# Revit family: 63__LF_UN_Emilux_Arrondi_R17
name_source: partatom
category: Lighting Fixtures
revit_build: Autodesk Revit 2017 (Build: 20190508_0315(x64)
units: mm (PartAtom-declared; Revit-internal decimal feet)

## family parameters
Always vertical = Yes
Cut with Voids When Loaded = No
Light Source = Yes
Part Type = Normal
Room Calculation Point = No
Round Connector Dimension = Use Diameter
Shared = No
Work Plane-Based = No

## types (9) — shared parameters
Assembly Code = 63.0
Color Filter = 16777215
Comment = Initial color needs to be filled in manually
Dali = Yes
Dimming Lamp Color Temperature Shift = <None>
Height Coupling = 24 mm  [stored 0.0787402 ft]
IP = IP 54
IfcExportAs = IfcLightFixtureType
IfcExportType = POINTSOURCE
Lamp = LED
Manufacturer = Emilux
Material = Polycarbonaat
Tilt Angle = 90.00°
URL = https://www.emilux.nl

## per-type parameters (varying)
| type | Apparent Load | Bottom Outside | Description | Emergency Lighting | Height Total | Length Coupling | Model | Photometric Web File | Ring ID | Ring OD | Top OD | Wattage Comments | Width Coupling |
| LED 1090lm 3000K (13W) | 13 VA | 61 mm | Cutout Ø130mm | No | 82 mm  [stored 0.269029 ft] | 75 mm | Arrondi+ Downlighter 13W | Arrondi 13W Alu 300K.ies | 121 mm | 145 mm | 48 mm  [stored 0.15748 ft] | 13W | 34 mm  [stored 0.111549 ft] |
| LED 2280lm 3000K (18W) | 25 VA | 97 mm | Cutout Ø205mm | No | 98 mm  [stored 0.321522 ft] | 120 mm  [stored 0.393701 ft] | Arrondi+ Downlighter 25W | Arrondi 25W Alu 3000K.ies | 173 mm  [stored 0.567585 ft] | 228 mm  [stored 0.748031 ft] | 73 mm  [stored 0.239501 ft] | 25W | 45 mm  [stored 0.147638 ft] |
| LED 1300lm 4000K (13W) | 13 VA | 61 mm | Cutout Ø130mm | No | 82 mm  [stored 0.269029 ft] | 75 mm | Arrondi+ Downlighter 13W | Arrondi 13W Alu 4000K.ies | 121 mm | 145 mm | 48 mm  [stored 0.15748 ft] | 13W | 34 mm  [stored 0.111549 ft] |
| LED 1300lm 6000K (13W) | 13 VA | 61 mm | Cutout Ø130mm | No | 82 mm  [stored 0.269029 ft] | 75 mm | Arrondi+ Downlighter 13W | Arrondi 13W Alu 6000K.ies | 121 mm | 145 mm | 48 mm  [stored 0.15748 ft] | 13W | 34 mm  [stored 0.111549 ft] |
| LED 1300lm 3000K (18W) | 18 VA | 61 mm | Cutout Ø130 | No | 82 mm  [stored 0.269029 ft] | 75 mm | Arrondi+ Downlighter 13W | Arrondi 18W Alu 3000K.ies | 121 mm | 145 mm | 48 mm  [stored 0.15748 ft] | 18W | 34 mm  [stored 0.111549 ft] |
| LED 2280lm 3000K (25W) + NV | 25 VA | 97 mm | Cutout Ø205mm | Yes | 98 mm  [stored 0.321522 ft] | 120 mm  [stored 0.393701 ft] | Arrondi+ Downlighter / NV 25W | Arrondi 25W Alu 3000K.ies | 173 mm  [stored 0.567585 ft] | 228 mm  [stored 0.748031 ft] | 73 mm  [stored 0.239501 ft] | 25W | 45 mm  [stored 0.147638 ft] |
| LED 2650lm 4000K (25W) | 25 VA | 97 mm | Cutout Ø205mm | No | 98 mm  [stored 0.321522 ft] | 120 mm  [stored 0.393701 ft] | Arrondi+ Downlighter 25W | Arrondi 25W Alu 4000K.ies | 173 mm  [stored 0.567585 ft] | 228 mm  [stored 0.748031 ft] | 73 mm  [stored 0.239501 ft] | 25W | 45 mm  [stored 0.147638 ft] |
| LED 2650lm 4000K (25W) + NV | 25 VA | 97 mm | Cutout Ø205mm | Yes | 98 mm  [stored 0.321522 ft] | 120 mm  [stored 0.393701 ft] | Arrondi+ Downlighter / NV 25W | Arrondi 25W Alu 4000K + NV.ies | 173 mm  [stored 0.567585 ft] | 228 mm  [stored 0.748031 ft] | 73 mm  [stored 0.239501 ft] | 25W | 45 mm  [stored 0.147638 ft] |
| LED 2650lm 6000K (25W) | 25 VA | 97 mm | Cutout Ø205mm | No | 98 mm  [stored 0.321522 ft] | 120 mm  [stored 0.393701 ft] | Arrondi+ Downlighter 25W | Arrondi 25W Alu 6000K.ies | 173 mm  [stored 0.567585 ft] | 228 mm  [stored 0.748031 ft] | 73 mm  [stored 0.239501 ft] | 25W | 45 mm  [stored 0.147638 ft] |

note: [stored X ft] marks values corroborated as IEEE doubles in the binary element streams (Revit-internal decimal feet)

## geometry (parser evidence)
native form markers: Sweep x3
no freeform markers — native parametric forms only
